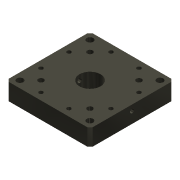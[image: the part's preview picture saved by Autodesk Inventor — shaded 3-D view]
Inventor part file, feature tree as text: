
AUTODESK INVENTOR PART (.ipt)
format: ipt  version: 2022 (Build 260153000, 153)  size: 181,248 bytes
history: native  units: mm
features: sketch x5, extrude x3, projected_geometry x3, reference x3, hole x2, other x2, chamfer x1, pattern_circular x1
ambient origin geometry x8: Origin, YZ Plane, XZ Plane, XY Plane, X Axis, Y Axis, Z Axis, Center Point
bodies: Solid1 (feature_tree)
feature tree (20):
  extrude  "Extrusion1"  Depth=60.0mm
  hole  "Hole1"  [1 undecoded]
  chamfer  "Chamfer1"  Distance=2.0mm Angle=45.0deg
  hole  "Hole2"  [1 undecoded]
  extrude  "Extrusion2"  Depth=10.0mm
  extrude  "Extrusion3"  Depth=10.0mm
  pattern_circular  "Circular Pattern1"  [2 undecoded]
  sketch  "Sketch1"  dims[d0=60.0mm d1=60.0mm]
  sketch  "Sketch2"  dims[d2=12.0mm d3=0.0mm d4=35.0mm]
  projected_geometry  "Projected Loop1"
  sketch  "Sketch3"  dims[d5=35.0mm]
  projected_geometry  "Projected Loop2"
  sketch  "Sketch4"  dims[d6=3.9mm d7=6.0mm d8=4.0mm d9=2.0mm d10=90.0deg d11=10.0mm d12=20.594885mm]
  projected_geometry  "Projected Loop3"
  reference  "Reference1"
  reference  "Reference2"
  reference  "Reference3"
  sketch  "Sketch5"  dims[d13=15.0mm d14=2.0mm d15=2.0mm d16=45.0deg d17=50.0mm d18=50.0mm d19=4.65mm d20=6.0mm d21=7.0mm d22=4.0mm d23=90.0deg d24=8.0mm d25=20.594885mm d26=3.0mm d27=4.0mm d28=30.0mm d29=10.0mm d30=0.0mm d31=2.9mm d32=2.9mm d33=15.0mm d34=15.0mm d35=2.9mm d36=2.9mm d37=10.0mm d38=0.0mm d39=20.0mm d40=90.0deg]
  other  "00_XY_stage-CHUO_SEIKI_LD-647-R1.iam"
  other  "00_XY_stage-CHUO_SEIKI_LD-647-R1-Bottom:1"
note: 4 required parameter values undecoded (feature->parameter linkage not recoverable at this tier; creation-order binding heuristic only, values carry confidence <= 0.55)
